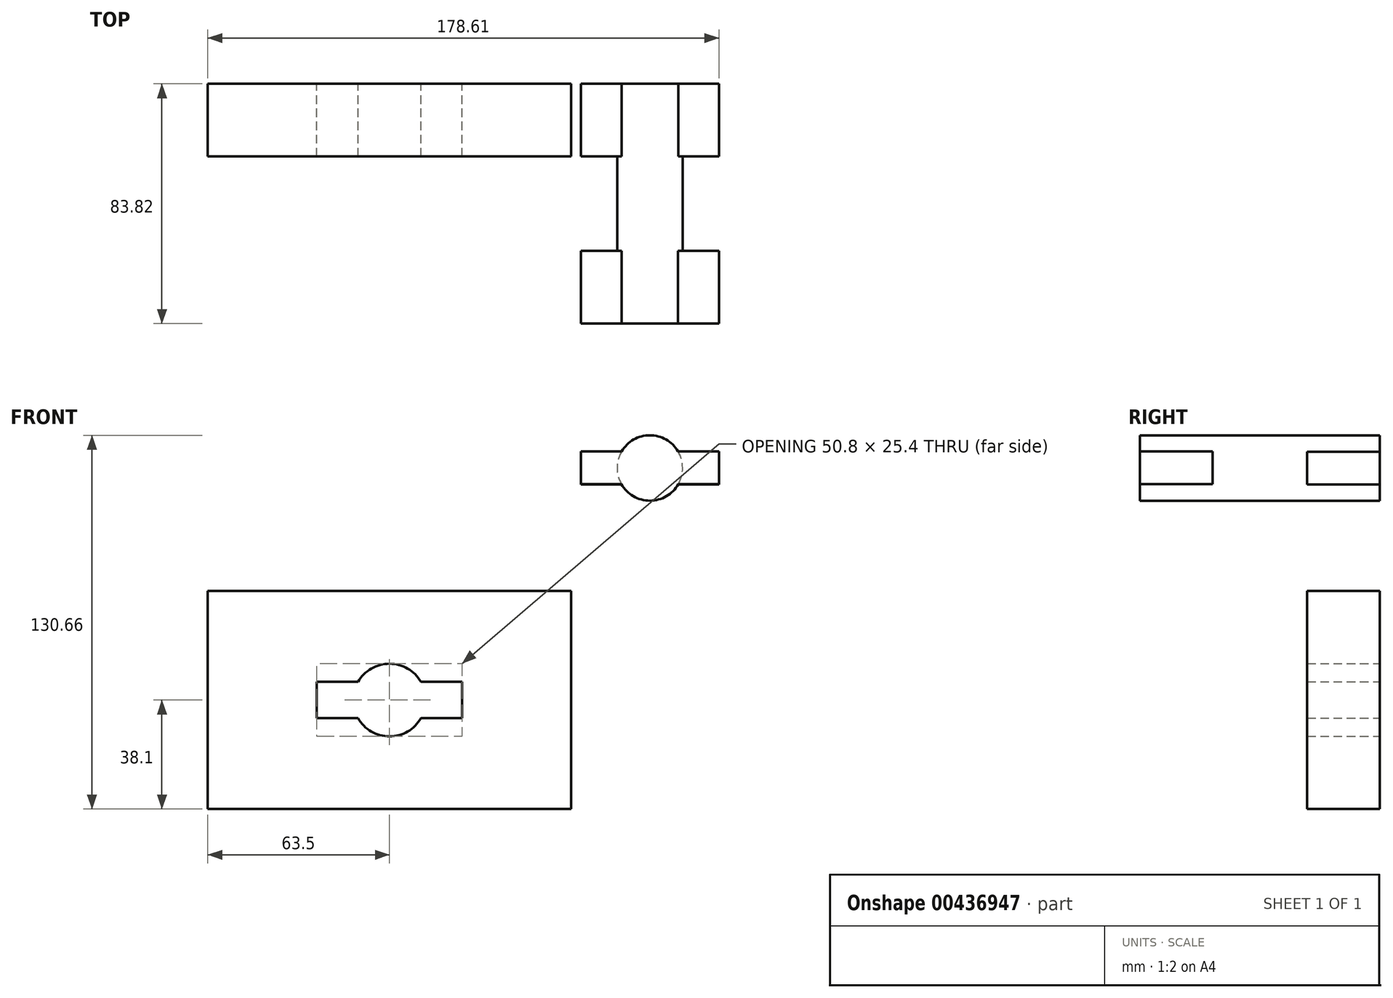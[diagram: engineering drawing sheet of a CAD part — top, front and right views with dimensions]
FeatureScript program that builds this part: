
annotation { "Feature Type Name" : "Feature", "Feature Type Description" : "" }
export const myFeature = defineFeature(function(context is Context, id is Id, definition is map)
    precondition{}
    {
        {
            var Q0;
            Q0=qCreatedBy(makeId("Front.planeOp"),FACE);
            var sketch = newSketch(context, id + "F0", { "sketchPlane" : qUnion([Q0])});
            skLineSegment(sketch, "E0.bottom", {"start": v(0, 0) * mm, "end": v(-127, 0) * mm});
            skLineSegment(sketch, "E0.top", {"start": v(0, -76.2) * mm, "end": v(-127, -76.2) * mm});
            skLineSegment(sketch, "E0.left", {"start": v(0, 0) * mm, "end": v(0, -76.2) * mm});
            skLineSegment(sketch, "E0.right", {"start": v(-127, 0) * mm, "end": v(-127, -76.2) * mm});
            skCircle(sketch, "E1", {"center": v(-63.5, -38.1) * mm, "radius": 12.7 * mm});
            skLineSegment(sketch, "E2", {"start": v(-52.5, -31.75) * mm, "end": v(-38.1, -31.75) * mm});
            skLineSegment(sketch, "E3", {"start": v(-38.1, -31.75) * mm, "end": v(-38.1, -44.45) * mm});
            skLineSegment(sketch, "E4", {"start": v(-38.1, -44.45) * mm, "end": v(-52.5, -44.45) * mm});
            skLineSegment(sketch, "E5", {"start": v(-74.5, -31.75) * mm, "end": v(-88.9, -31.75) * mm});
            skLineSegment(sketch, "E6", {"start": v(-88.9, -31.75) * mm, "end": v(-88.9, -44.45) * mm});
            skLineSegment(sketch, "E7", {"start": v(-88.9, -44.45) * mm, "end": v(-74.5, -44.45) * mm});
            skSolve(sketch);
        }
        {
            var Q0;
            Q0=makeQuery(id+"F0.imprint","IMPRINT",FACE,{"disambiguationData":[TD([[makeQuery(id+"F0.imprint","IMPRINT",EDGE,{"derivedFrom":sQuery(id+"F0.wireOp",EDGE,"E0.bottom")}),1.0]])]});
            extrude(context, id + "F1", {"entities" : qUnion([Q0]), "depth" : 25.4 * mm});
        }
        {
            var Q0;
            Q0=makeQuery(id+"F0.imprint","IMPRINT",FACE,{"disambiguationData":[TD([[makeQuery(id+"F0.imprint","IMPRINT",EDGE,{"derivedFrom":sQuery(id+"F0.wireOp",EDGE,"E0.bottom")}),1.0]])]});
            extrude(context, id + "F2", {"entities" : qUnion([Q0]), "operationType" : NewBodyOperationType.ADD, "depth" : 25.4 * mm});
        }
        {
            var Q0;
            Q0=qCreatedBy(makeId("Front.planeOp"),FACE);
            var sketch = newSketch(context, id + "F3", { "sketchPlane" : qUnion([Q0])});
            skCircle(sketch, "E8", {"center": v(27.48, 43.03) * mm, "radius": 11.43 * mm});
            skLineSegment(sketch, "E9.bottom", {"start": v(3.35, 37.31) * mm, "end": v(51.61, 37.31) * mm});
            skLineSegment(sketch, "E9.top", {"start": v(3.35, 48.74) * mm, "end": v(51.61, 48.74) * mm});
            skLineSegment(sketch, "E9.left", {"start": v(3.35, 37.31) * mm, "end": v(3.35, 48.74) * mm});
            skLineSegment(sketch, "E9.right", {"start": v(51.61, 37.31) * mm, "end": v(51.61, 48.74) * mm});
            skSolve(sketch);
        }
        {
            var Q0;
            {var subQ5=sQuery(id+"F3.wireOp",EDGE,"E9.right");Q0=makeQuery(id+"F3.imprint","IMPRINT",FACE,{"disambiguationData":[TD([[makeQuery(id+"F3.imprint","IMPRINT",EDGE,{"derivedFrom":subQ5}),1.0]])]});}
            var Q1;
            {var subQ0=sQuery(id+"F3.wireOp",EDGE,"E9.top");var subQ1=sQuery(id+"F3.wireOp",EDGE,"E8");var subQ2=makeQuery(id+"F3.imprint","INTERSECT",VERTEX,{"disambiguationData":[OD(0.0)],"derivedFrom":[subQ1,subQ0]});Q1=makeQuery(id+"F3.imprint","IMPRINT",FACE,{"disambiguationData":[TD([[makeQuery(id+"F3.imprint","IMPRINT",EDGE,{"disambiguationData":[TD([[subQ2,-1.0]])],"derivedFrom":subQ1}),1.0]])]});}
            var Q2;
            {var subQ0=sQuery(id+"F3.wireOp",EDGE,"E9.bottom");var subQ1=sQuery(id+"F3.wireOp",EDGE,"E8");var subQ2=makeQuery(id+"F3.imprint","INTERSECT",VERTEX,{"disambiguationData":[OD(0.0)],"derivedFrom":[subQ1,subQ0]});Q2=makeQuery(id+"F3.imprint","IMPRINT",FACE,{"disambiguationData":[TD([[makeQuery(id+"F3.imprint","IMPRINT",EDGE,{"disambiguationData":[TD([[subQ2,-1.0]])],"derivedFrom":subQ1}),1.0]])]});}
            var Q3;
            {var subQ0=sQuery(id+"F3.wireOp",EDGE,"E9.top");var subQ1=sQuery(id+"F3.wireOp",EDGE,"E8");var subQ2=makeQuery(id+"F3.imprint","INTERSECT",VERTEX,{"disambiguationData":[OD(0.0)],"derivedFrom":[subQ1,subQ0]});Q3=makeQuery(id+"F3.imprint","IMPRINT",FACE,{"disambiguationData":[TD([[makeQuery(id+"F3.imprint","IMPRINT",EDGE,{"disambiguationData":[TD([[subQ2,1.0]])],"derivedFrom":subQ1}),1.0]])]});}
            var Q4;
            {var subQ5=sQuery(id+"F3.wireOp",EDGE,"E9.left");Q4=makeQuery(id+"F3.imprint","IMPRINT",FACE,{"disambiguationData":[TD([[makeQuery(id+"F3.imprint","IMPRINT",EDGE,{"derivedFrom":subQ5}),-1.0]])]});}
            extrude(context, id + "F4", {"entities" : qUnion([Q0, Q1, Q2, Q3, Q4]), "depth" : 25.4 * mm});
        }
        {
            var Q0;
            Q0=makeQuery(id+"F4.opExtrude","CAP_FACE",FACE,{"disambiguationData":[OSD([sQuery(id+"F3.wireOp",EDGE,"E8")])],"isStart":false});
            var sketch = newSketch(context, id + "F5", { "sketchPlane" : qUnion([Q0])});
            skPoint(sketch, "E10.center.orphan", {"position": v(27.48, 43.03) * mm});
            skCircle(sketch, "E11", {"center": v(27.48, 43.03) * mm, "radius": 11.43 * mm});
            skSolve(sketch);
        }
        {
            var Q0;
            Q0 = qSketchRegion(id + "F5", true);
            extrude(context, id + "F6", {"entities" : qUnion([Q0]), "operationType" : NewBodyOperationType.ADD, "depth" : 33.02 * mm});
        }
        {
            var Q0;
            Q0=makeQuery(id+"F6.opExtrude","CAP_FACE",FACE,{"disambiguationData":[OSD([sQuery(id+"F5.wireOp",EDGE,"E11")])],"isStart":false});
            var sketch = newSketch(context, id + "F7", { "sketchPlane" : qUnion([Q0])});
            skLineSegment(sketch, "E12", {"start": v(37.32, 48.85) * mm, "end": v(51.61, 48.85) * mm});
            skLineSegment(sketch, "E13", {"start": v(37.44, 37.42) * mm, "end": v(51.61, 37.42) * mm});
            skLineSegment(sketch, "E14", {"start": v(51.61, 37.42) * mm, "end": v(51.61, 48.85) * mm});
            skLineSegment(sketch, "E15", {"start": v(17.53, 37.42) * mm, "end": v(3.35, 37.42) * mm});
            skLineSegment(sketch, "E16", {"start": v(17.64, 48.85) * mm, "end": v(3.35, 48.85) * mm});
            skLineSegment(sketch, "E17", {"start": v(3.35, 48.85) * mm, "end": v(3.35, 37.42) * mm});
            skCircle(sketch, "E18", {"center": v(27.48, 43.03) * mm, "radius": 11.43 * mm});
            skSolve(sketch);
        }
        {
            var Q0;
            {var subQ0=sQuery(id+"F7.wireOp",EDGE,"E12");Q0=makeQuery(id+"F7.imprint","IMPRINT",FACE,{"disambiguationData":[TD([[makeQuery(id+"F7.imprint","IMPRINT",EDGE,{"derivedFrom":subQ0}),-1.0]])]});}
            var Q1;
            {var subQ0=sQuery(id+"F7.wireOp",EDGE,"E15");Q1=makeQuery(id+"F7.imprint","IMPRINT",FACE,{"disambiguationData":[TD([[makeQuery(id+"F7.imprint","IMPRINT",EDGE,{"derivedFrom":subQ0}),-1.0]])]});}
            var Q2;
            {var subQ0=sQuery(id+"F7.wireOp",EDGE,"E18");var subQ1=makeQuery(id+"F7.imprint","INTERSECT",VERTEX,{"derivedFrom":[sQuery(id+"F7.wireOp",EDGE,"E12"),subQ0]});Q2=makeQuery(id+"F7.imprint","IMPRINT",FACE,{"disambiguationData":[TD([[makeQuery(id+"F7.imprint","IMPRINT",EDGE,{"disambiguationData":[TD([[subQ1,-1.0]])],"derivedFrom":subQ0}),1.0]])]});}
            extrude(context, id + "F8", {"entities" : qUnion([Q0, Q1, Q2]), "operationType" : NewBodyOperationType.ADD, "depth" : 25.4 * mm});
        }
    });
